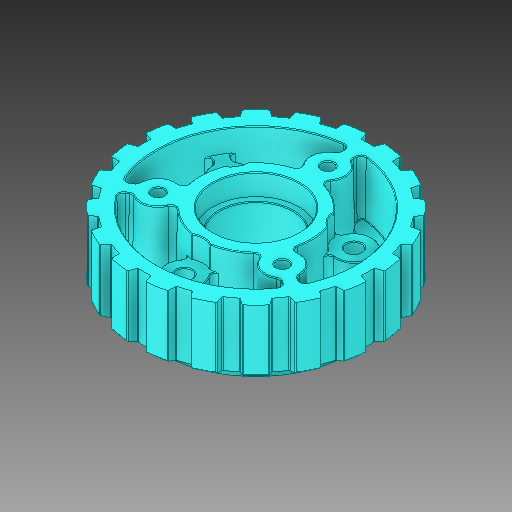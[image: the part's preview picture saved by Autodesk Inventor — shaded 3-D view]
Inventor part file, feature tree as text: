
AUTODESK INVENTOR PART (.ipt)
format: ipt  version: 2019 (Build 230136000, 136)  size: 1,391,616 bytes
history: native  units: in
note: dims shown in document units (in); Inventor stores cm internally (conversion verified against a paired STEP export)
features: fillet x1
ambient origin geometry x8: Origin, YZ Plane, XZ Plane, XY Plane, X Axis, Y Axis, Z Axis, Center Point
bodies: Solid1 (feature_tree)
feature tree (1):
  fillet  "Fillet4"  [1 undecoded]
note: 1 required parameter value undecoded (feature->parameter linkage not recoverable at this tier; creation-order binding heuristic only, values carry confidence <= 0.55)
